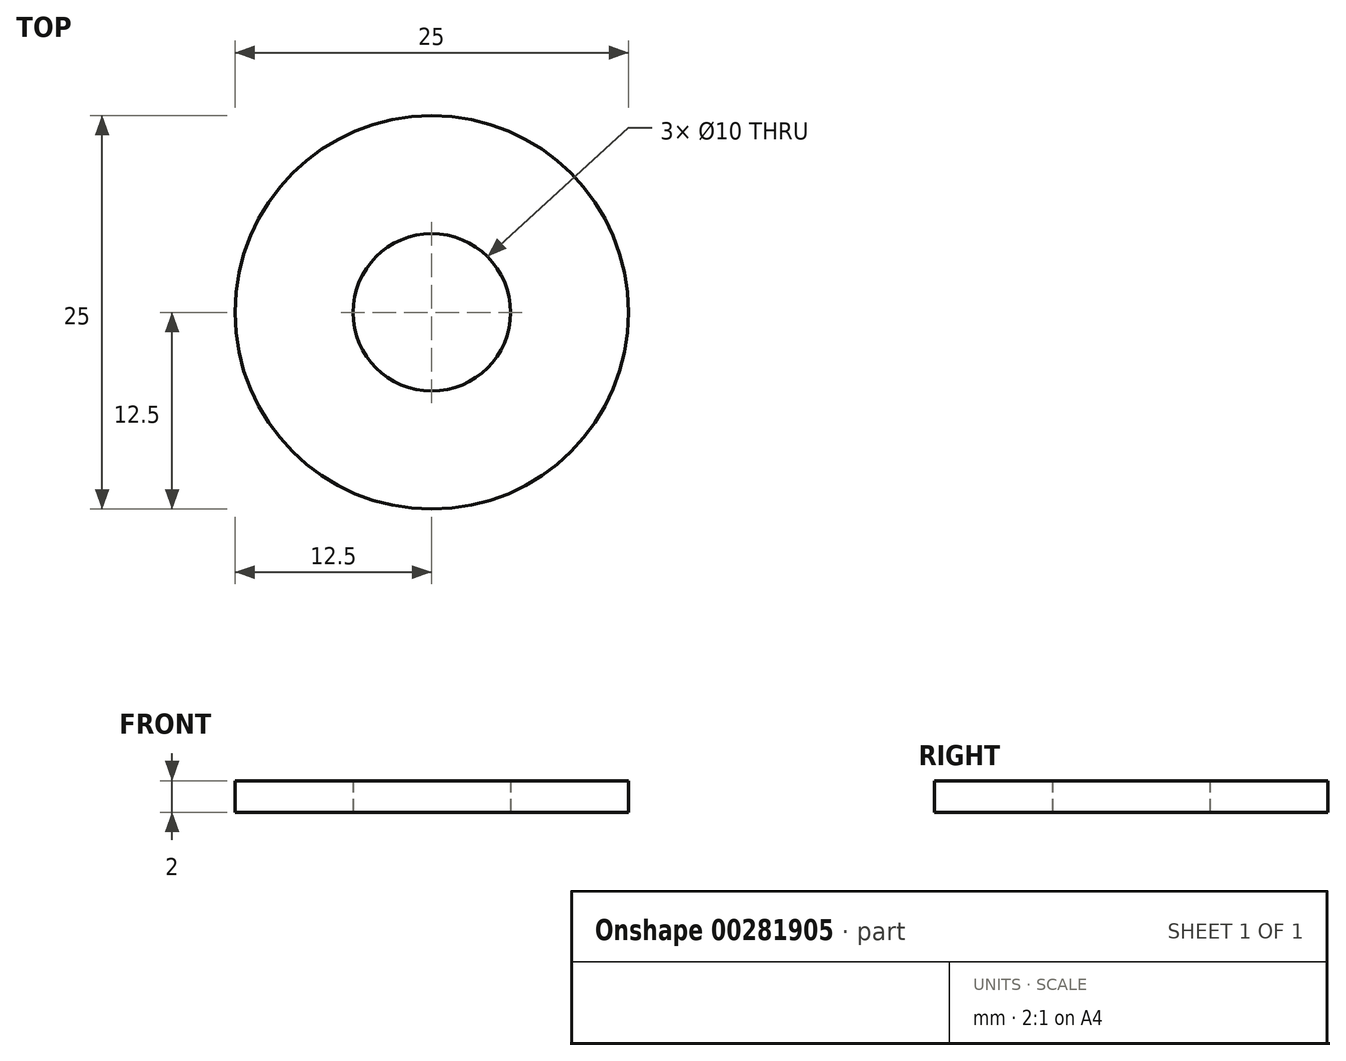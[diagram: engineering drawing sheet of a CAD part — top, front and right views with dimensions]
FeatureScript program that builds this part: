
annotation { "Feature Type Name" : "Feature", "Feature Type Description" : "" }
export const myFeature = defineFeature(function(context is Context, id is Id, definition is map)
    precondition{}
    {
        {
            var Q0;
            Q0=qCreatedBy(makeId("Top.planeOp"),FACE);
            var sketch = newSketch(context, id + "F0", { "sketchPlane" : qUnion([Q0])});
            skCircle(sketch, "E0", {"center": v(0, 0) * mm, "radius": 12.5 * mm});
            skCircle(sketch, "E1", {"center": v(0, 0) * mm, "radius": 5 * mm});
            skSolve(sketch);
        }
        {
            var Q0;
            Q0=qSketchRegion(id+"F0",true);
            extrude(context, id + "F1", {"entities" : qUnion([Q0]), "depth" : 2 * mm});
        }
    });
